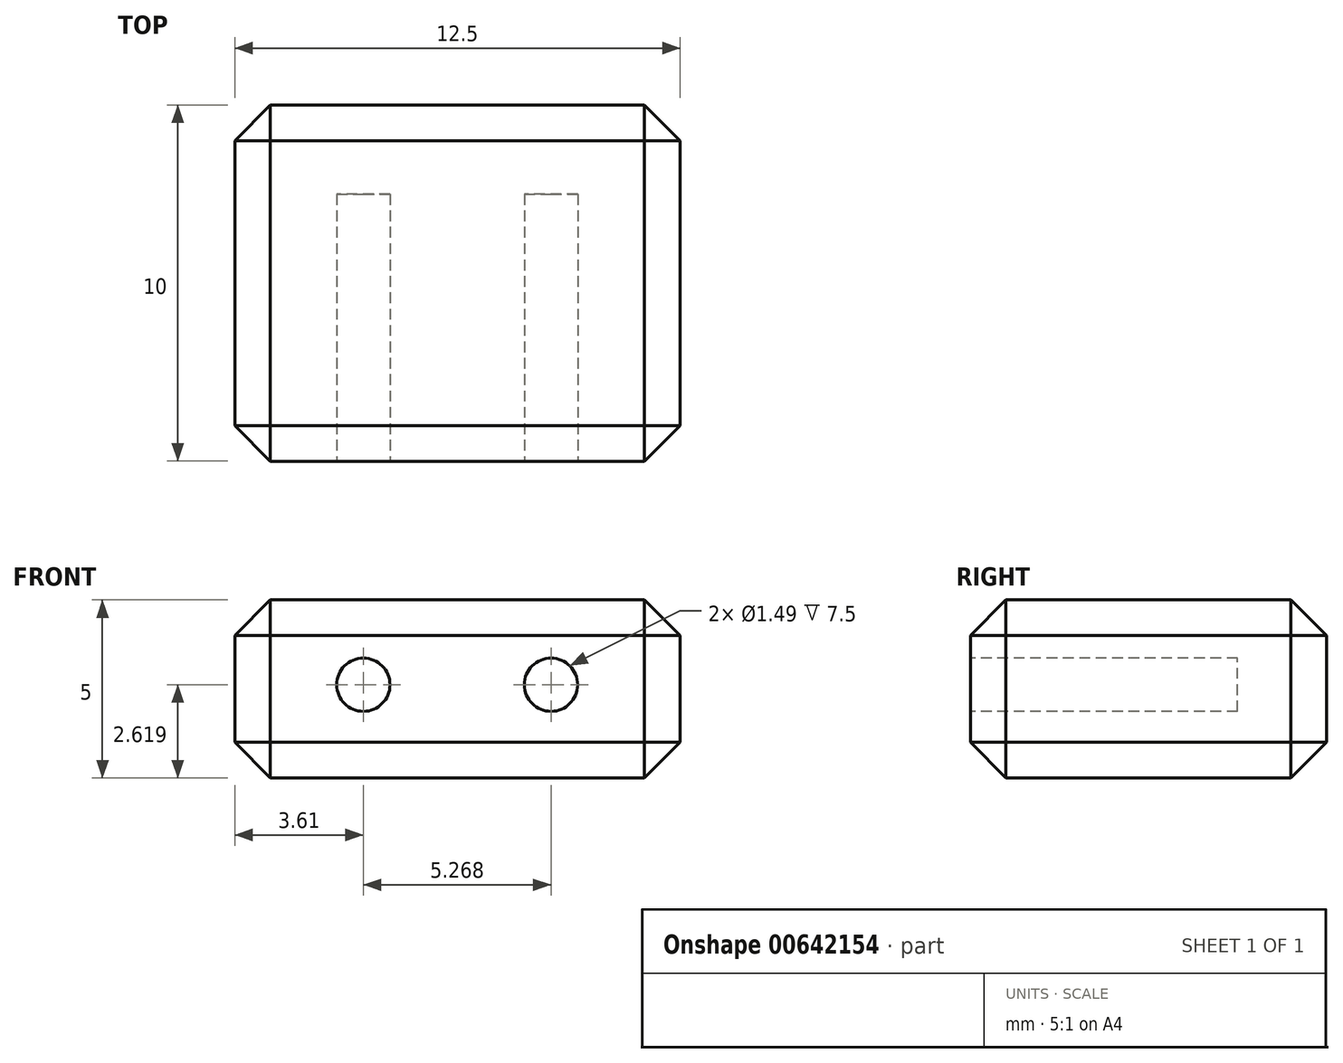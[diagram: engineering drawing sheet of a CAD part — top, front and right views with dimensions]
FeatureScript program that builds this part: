
annotation { "Feature Type Name" : "Feature", "Feature Type Description" : "" }
export const myFeature = defineFeature(function(context is Context, id is Id, definition is map)
    precondition{}
    {
        {
            var Q0;
            Q0=qCreatedBy(makeId("Top.planeOp"),FACE);
            var sketch = newSketch(context, id + "F0", { "sketchPlane" : qUnion([Q0])});
            skLineSegment(sketch, "E0.bottom", {"start": v(-3.03, -1.92) * mm, "end": v(9.47, -1.92) * mm});
            skLineSegment(sketch, "E0.top", {"start": v(-3.03, -11.92) * mm, "end": v(9.47, -11.92) * mm});
            skLineSegment(sketch, "E0.left", {"start": v(-3.03, -1.92) * mm, "end": v(-3.03, -11.92) * mm});
            skLineSegment(sketch, "E0.right", {"start": v(9.47, -1.92) * mm, "end": v(9.47, -11.92) * mm});
            skLineSegment(sketch, "E1.left", {"start": v(-3.03, -11.92) * mm, "end": v(-3.03, -6.92) * mm});
            skSolve(sketch);
        }
        {
            var Q0;
            Q0=makeQuery(id+"F0.imprint","IMPRINT",FACE,{"disambiguationData":[TD([[makeQuery(id+"F0.imprint","IMPRINT",EDGE,{"derivedFrom":sQuery(id+"F0.wireOp",EDGE,"E0.left")}),-1.0]])]});
            var Q1;
            Q1=makeQuery(id+"F0.imprint","IMPRINT",FACE,{"disambiguationData":[TD([[makeQuery(id+"F0.imprint","IMPRINT",EDGE,{"derivedFrom":sQuery(id+"F0.wireOp",EDGE,"E0.bottom")}),-1.0]])]});
            extrude(context, id + "F1", {"entities" : qUnion([Q0, Q1]), "depth" : 5 * mm, "offsetDistance" : 25.4 * mm});
        }
        {
            var Q0;
            Q0=makeQuery(id+"F1.opExtrude","SWEPT_FACE",FACE,{"disambiguationData":[OSD([sQuery(id+"F0.wireOp",EDGE,"E0.top")])]});
            var sketch = newSketch(context, id + "F2", { "sketchPlane" : qUnion([Q0])});
            skSolve(sketch);
        }
        {
            var Q0;
            Q0=makeQuery(id+"F1.opExtrude","CAP_EDGE",EDGE,{"disambiguationData":[OSD([sQuery(id+"F0.wireOp",EDGE,"E0.top")])],"isStart":false});
            var Q1;
            Q1=makeQuery(id+"F1.opExtrude","CAP_EDGE",EDGE,{"disambiguationData":[OSD([sQuery(id+"F0.wireOp",EDGE,"E0.right")])],"isStart":false});
            var Q2;
            Q2=makeQuery(id+"FKgUUPM6xCZ4TZf_1.opChamfer","BLEND_EDGE",EDGE,{"blendedFrom":[makeQuery(id+"F1.opExtrude","SWEPT_EDGE",EDGE,{"disambiguationData":[OSD([sQuery(id+"F0.wireOp",EDGE,"PRfnEaRS-T7vr-Rmg5-DXbl-tRGKBbvwYH9x"),sQuery(id+"F0.wireOp",EDGE,"u6btSIih-0wHW-6TSG-opwj-zz3jc8rJvWwZ")])]}),makeQuery(id+"F1.opExtrude","SWEPT_FACE",FACE,{"disambiguationData":[OSD([sQuery(id+"F0.wireOp",EDGE,"E1.left")])]})],"blendedInto":[makeQuery(id+"F1.opExtrude","SWEPT_FACE",FACE,{"disambiguationData":[OSD([sQuery(id+"F0.wireOp",EDGE,"E1.left")])]})]});
            var Q3;
            {var subQ0=sQuery(id+"F0.wireOp",EDGE,"PRfnEaRS-T7vr-Rmg5-DXbl-tRGKBbvwYH9x");Q3=makeQuery(id+"FKgUUPM6xCZ4TZf_1.opChamfer","BLEND_EDGE",EDGE,{"blendedFrom":[makeQuery(id+"F1.opExtrude","SWEPT_EDGE",EDGE,{"disambiguationData":[OSD([subQ0,sQuery(id+"F0.wireOp",EDGE,"u6btSIih-0wHW-6TSG-opwj-zz3jc8rJvWwZ")])]}),makeQuery(id+"F1.opExtrude","SWEPT_FACE",FACE,{"disambiguationData":[OSD([subQ0])]})],"blendedInto":[makeQuery(id+"F1.opExtrude","SWEPT_FACE",FACE,{"disambiguationData":[OSD([subQ0])]})]});}
            var Q4;
            {var subQ0=sQuery(id+"F0.wireOp",EDGE,"u6btSIih-0wHW-6TSG-opwj-zz3jc8rJvWwZ");var subQ1=sQuery(id+"F0.wireOp",EDGE,"PRfnEaRS-T7vr-Rmg5-DXbl-tRGKBbvwYH9x");Q4=makeQuery(id+"FKgUUPM6xCZ4TZf_1.opChamfer","BLEND_EDGE",EDGE,{"blendedFrom":[makeQuery(id+"F1.opExtrude","SWEPT_EDGE",EDGE,{"disambiguationData":[OSD([subQ1,subQ0])]}),makeQuery(id+"F1.opExtrude","CAP_FACE",FACE,{"disambiguationData":[OSD([sQuery(id+"F0.wireOp",EDGE,"E0.bottom"),sQuery(id+"F0.wireOp",EDGE,"E0.top"),sQuery(id+"F0.wireOp",EDGE,"E0.right"),sQuery(id+"F0.wireOp",EDGE,"E1.left"),subQ1,subQ0])],"isStart":false})],"blendedInto":[makeQuery(id+"F1.opExtrude","CAP_FACE",FACE,{"disambiguationData":[OSD([sQuery(id+"F0.wireOp",EDGE,"E0.bottom"),sQuery(id+"F0.wireOp",EDGE,"E0.top"),sQuery(id+"F0.wireOp",EDGE,"E0.right"),sQuery(id+"F0.wireOp",EDGE,"E1.left"),subQ1,subQ0])],"isStart":false})]});}
            var Q5;
            {var subQ0=sQuery(id+"F0.wireOp",EDGE,"u6btSIih-0wHW-6TSG-opwj-zz3jc8rJvWwZ");var subQ1=sQuery(id+"F0.wireOp",EDGE,"PRfnEaRS-T7vr-Rmg5-DXbl-tRGKBbvwYH9x");Q5=makeQuery(id+"FKgUUPM6xCZ4TZf_1.opChamfer","BLEND_EDGE",EDGE,{"blendedFrom":[makeQuery(id+"F1.opExtrude","SWEPT_EDGE",EDGE,{"disambiguationData":[OSD([subQ1,subQ0])]}),makeQuery(id+"F1.opExtrude","CAP_FACE",FACE,{"disambiguationData":[OSD([sQuery(id+"F0.wireOp",EDGE,"E0.bottom"),sQuery(id+"F0.wireOp",EDGE,"E0.top"),sQuery(id+"F0.wireOp",EDGE,"E0.right"),sQuery(id+"F0.wireOp",EDGE,"E1.left"),subQ1,subQ0])],"isStart":true})],"blendedInto":[makeQuery(id+"F1.opExtrude","CAP_FACE",FACE,{"disambiguationData":[OSD([sQuery(id+"F0.wireOp",EDGE,"E0.bottom"),sQuery(id+"F0.wireOp",EDGE,"E0.top"),sQuery(id+"F0.wireOp",EDGE,"E0.right"),sQuery(id+"F0.wireOp",EDGE,"E1.left"),subQ1,subQ0])],"isStart":true})]});}
            var Q6;
            Q6=makeQuery(id+"F1.opExtrude","CAP_EDGE",EDGE,{"disambiguationData":[OSD([sQuery(id+"F0.wireOp",EDGE,"PRfnEaRS-T7vr-Rmg5-DXbl-tRGKBbvwYH9x")])],"isStart":true});
            var Q7;
            Q7=makeQuery(id+"F1.opExtrude","CAP_EDGE",EDGE,{"disambiguationData":[OSD([sQuery(id+"F0.wireOp",EDGE,"PRfnEaRS-T7vr-Rmg5-DXbl-tRGKBbvwYH9x")])],"isStart":false});
            var Q8;
            Q8=makeQuery(id+"F1.opExtrude","SWEPT_EDGE",EDGE,{"disambiguationData":[OSD([sQuery(id+"F0.wireOp",EDGE,"E0.bottom"),sQuery(id+"F0.wireOp",EDGE,"E0.left"),sQuery(id+"F0.wireOp",EDGE,"PRfnEaRS-T7vr-Rmg5-DXbl-tRGKBbvwYH9x")])]});
            var Q9;
            Q9=makeQuery(id+"F1.opExtrude","SWEPT_EDGE",EDGE,{"disambiguationData":[OSD([sQuery(id+"F0.wireOp",EDGE,"E0.top"),sQuery(id+"F0.wireOp",EDGE,"E1.left")])]});
            var Q10;
            Q10=makeQuery(id+"F1.opExtrude","SWEPT_EDGE",EDGE,{"disambiguationData":[OSD([sQuery(id+"F0.wireOp",EDGE,"E0.top"),sQuery(id+"F0.wireOp",EDGE,"E0.right")])]});
            var Q11;
            Q11=makeQuery(id+"F1.opExtrude","CAP_EDGE",EDGE,{"disambiguationData":[OSD([sQuery(id+"F0.wireOp",EDGE,"E0.right")])],"isStart":true});
            var Q12;
            Q12=makeQuery(id+"F1.opExtrude","CAP_EDGE",EDGE,{"disambiguationData":[OSD([sQuery(id+"F0.wireOp",EDGE,"E0.top")])],"isStart":true});
            var Q13;
            Q13=makeQuery(id+"F1.opExtrude","SWEPT_EDGE",EDGE,{"disambiguationData":[OSD([sQuery(id+"F0.wireOp",EDGE,"E0.bottom"),sQuery(id+"F0.wireOp",EDGE,"E0.right")])]});
            var Q14;
            Q14=makeQuery(id+"F1.opExtrude","CAP_EDGE",EDGE,{"disambiguationData":[OSD([sQuery(id+"F0.wireOp",EDGE,"E0.left"),sQuery(id+"F0.wireOp",EDGE,"E1.left")])],"isStart":false});
            var Q15;
            Q15=makeQuery(id+"F1.opExtrude","CAP_EDGE",EDGE,{"disambiguationData":[OSD([sQuery(id+"F0.wireOp",EDGE,"E0.bottom")])],"isStart":false});
            var Q16;
            Q16=makeQuery(id+"F1.opExtrude","CAP_EDGE",EDGE,{"disambiguationData":[OSD([sQuery(id+"F0.wireOp",EDGE,"E0.bottom")])],"isStart":true});
            var Q17;
            Q17=makeQuery(id+"F1.opExtrude","CAP_EDGE",EDGE,{"disambiguationData":[OSD([sQuery(id+"F0.wireOp",EDGE,"E0.left"),sQuery(id+"F0.wireOp",EDGE,"E1.left")])],"isStart":true});
            chamfer(context, id + "F3", {"entities" : qUnion([Q0, Q1, Q2, Q3, Q4, Q5, Q6, Q7, Q8, Q9, Q10, Q11, Q12, Q13, Q14, Q15, Q16, Q17]), "width" : 1 * mm, "tangentPropagation" : true});
        }
        {
            var Q0;
            {var subQ0=sQuery(id+"F0.wireOp",EDGE,"E0.top");Q0=makeQuery(id+"F2.imprint","IMPRINT",FACE,{"disambiguationData":[TD([[makeQuery(id+"F2.imprint","IMPRINT",EDGE,{"derivedFrom":makeQuery(id+"F1.opExtrude","CAP_EDGE",EDGE,{"disambiguationData":[OSD([subQ0])],"isStart":true})}),1.0]])]});}
            var sketch = newSketch(context, id + "F4", { "sketchPlane" : qUnion([Q0])});
            skCircle(sketch, "E2", {"center": v(0.58, 2.62) * mm, "radius": 0.75 * mm});
            skCircle(sketch, "E3", {"center": v(5.85, 2.62) * mm, "radius": 0.75 * mm});
            skSolve(sketch);
        }
        {
            var Q0;
            Q0=qSketchRegion(id+"F4",true);
            extrude(context, id + "F5", {"entities" : qUnion([Q0]), "operationType" : NewBodyOperationType.REMOVE, "oppositeDirection" : true, "depth" : 7.5 * mm, "offsetDistance" : 25.4 * mm});
        }
    });
